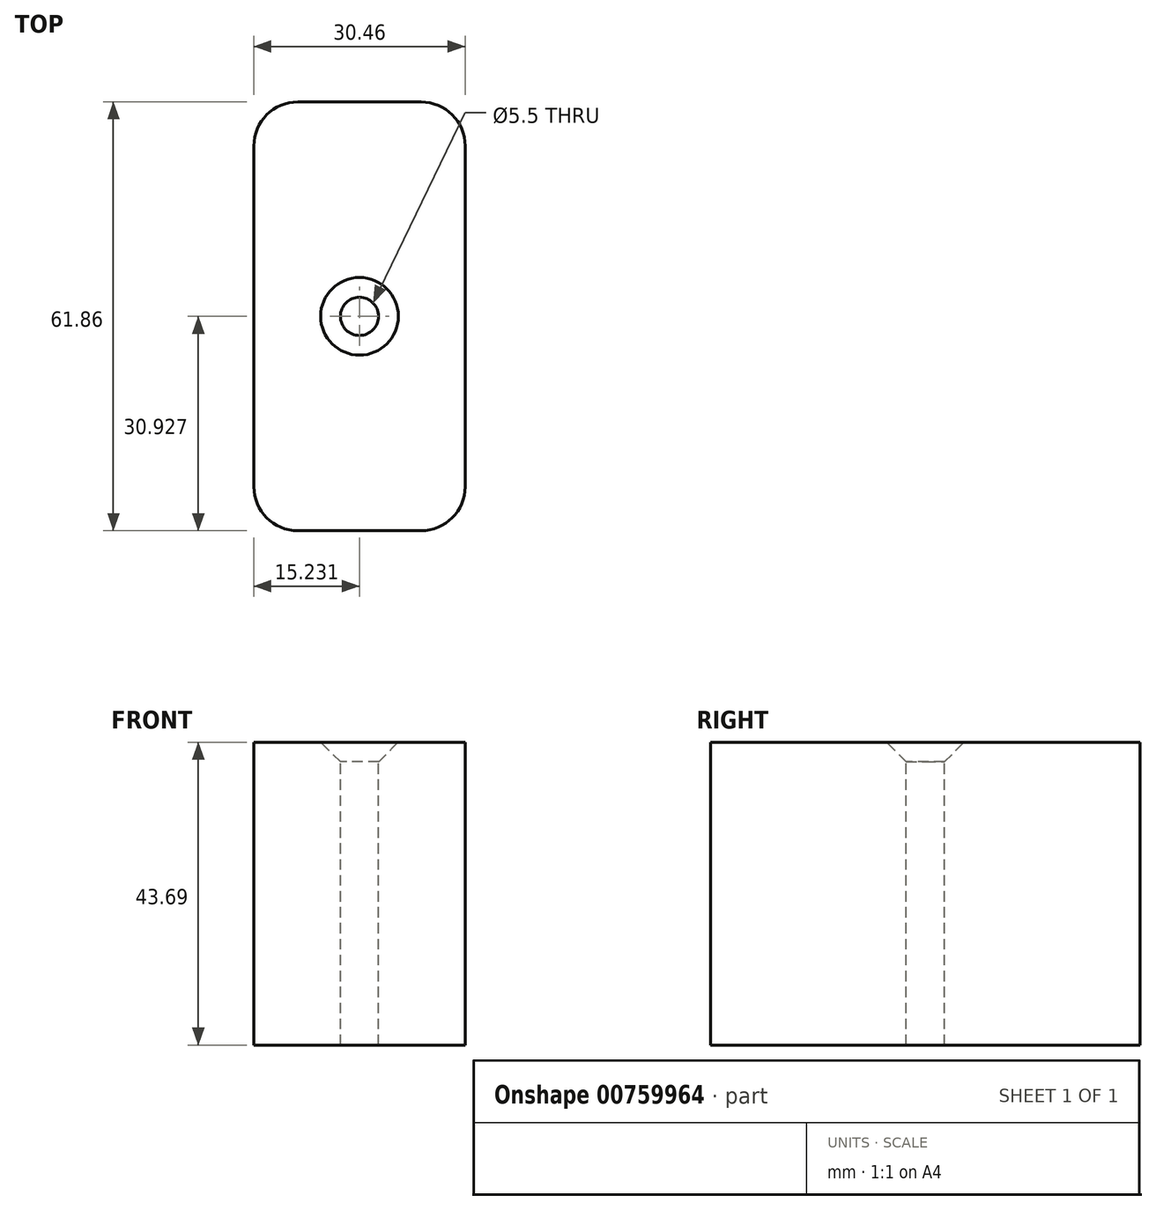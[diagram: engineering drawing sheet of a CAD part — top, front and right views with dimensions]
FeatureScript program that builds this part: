
annotation { "Feature Type Name" : "Feature", "Feature Type Description" : "" }
export const myFeature = defineFeature(function(context is Context, id is Id, definition is map)
    precondition{}
    {
        {
            var Q0;
            Q0=qCreatedBy(makeId("Top.planeOp"),FACE);
            var sketch = newSketch(context, id + "F0", { "sketchPlane" : qUnion([Q0])});
            skLineSegment(sketch, "E0.bottom", {"start": v(-34.76, 28) * mm, "end": v(-17, 28) * mm});
            skLineSegment(sketch, "E0.top", {"start": v(-34.76, -33.85) * mm, "end": v(-17, -33.85) * mm});
            skLineSegment(sketch, "E0.left", {"start": v(-41.1, 21.66) * mm, "end": v(-41.1, -27.5) * mm});
            skLineSegment(sketch, "E0.right", {"start": v(-10.65, 21.66) * mm, "end": v(-10.65, -27.5) * mm});
            skPoint(sketch, "E1.visualSharp", {"position": v(-41.1, 28) * mm});
            skArc(sketch, "E1.filletArc", {"start": v(-34.76, 28) * mm, "mid": v(-39.25, 26.15) * mm, "end": v(-41.1, 21.66) * mm});
            skPoint(sketch, "E2.visualSharp", {"position": v(-10.65, 28) * mm});
            skArc(sketch, "E2.filletArc", {"start": v(-10.65, 21.66) * mm, "mid": v(-12.51, 26.15) * mm, "end": v(-17, 28) * mm});
            skPoint(sketch, "E3.visualSharp", {"position": v(-10.65, -33.85) * mm});
            skArc(sketch, "E3.filletArc", {"start": v(-17, -33.85) * mm, "mid": v(-12.51, -32) * mm, "end": v(-10.65, -27.5) * mm});
            skPoint(sketch, "E4.visualSharp", {"position": v(-41.1, -33.85) * mm});
            skArc(sketch, "E4.filletArc", {"start": v(-41.1, -27.5) * mm, "mid": v(-39.25, -32) * mm, "end": v(-34.76, -33.85) * mm});
            skLineSegment(sketch, "E5", {"start": v(-41.1, 28) * mm, "end": v(-10.65, -33.85) * mm, "construction": true});
            skLineSegment(sketch, "E6", {"start": v(-25.88, -2.92) * mm, "end": v(-10.65, 28) * mm, "construction": true});
            skLineSegment(sketch, "E7", {"start": v(-25.88, -2.92) * mm, "end": v(-41.1, -33.85) * mm, "construction": true});
            skSolve(sketch);
        }
        {
            var Q0;
            Q0=makeQuery(id+"F0.imprint","IMPRINT",FACE,{"disambiguationData":[TD([[makeQuery(id+"F0.imprint","IMPRINT",EDGE,{"derivedFrom":sQuery(id+"F0.wireOp",EDGE,"E0.bottom")}),-1.0]])]});
            extrude(context, id + "F1", {"entities" : qUnion([Q0]), "oppositeDirection" : true, "depth" : 43.69 * mm, "offsetDistance" : 25.4 * mm});
        }
        {
            var Q0;
            Q0=sQuery(id+"F0.wireOp",VERTEX,"E6.start");
            var Q1;
            Q1=makeQuery(id+"F1.opExtrude","SWEPT_BODY",BODY,{"disambiguationData":[OSD([sQuery(id+"F0.wireOp",EDGE,"E0.bottom"),sQuery(id+"F0.wireOp",EDGE,"E0.top"),sQuery(id+"F0.wireOp",EDGE,"E0.left"),sQuery(id+"F0.wireOp",EDGE,"E0.right"),sQuery(id+"F0.wireOp",EDGE,"E1.filletArc"),sQuery(id+"F0.wireOp",EDGE,"E2.filletArc"),sQuery(id+"F0.wireOp",EDGE,"E3.filletArc"),sQuery(id+"F0.wireOp",EDGE,"E4.filletArc")])]});
            hole(context, id + "F2", {"style" : HoleStyle.C_SINK, "endStyle" : HoleEndStyle.THROUGH, "standardTappedOrClearance" : lookupTablePath({ "standard" : "ISO", "fit" : "Normal", "size" : "M5", "type" : "Clearance" }), "standardBlindInLast" : lookupTablePath({ "fit" : "Standard", "standard" : "ISO", "size" : "M5", "type" : "Clearance" }), "holeDiameter" : 5.5 * mm, "cSinkDiameter" : 11.2 * mm, "cSinkAngle" : 90 * degree, "majorDiameter" : 6.35 * mm, "isTappedThrough" : true, "tappedDepth" : 12.7 * mm, "tapClearance" : 3, "locations" : qUnion([Q0]), "scope" : qUnion([Q1])});
        }
    });
